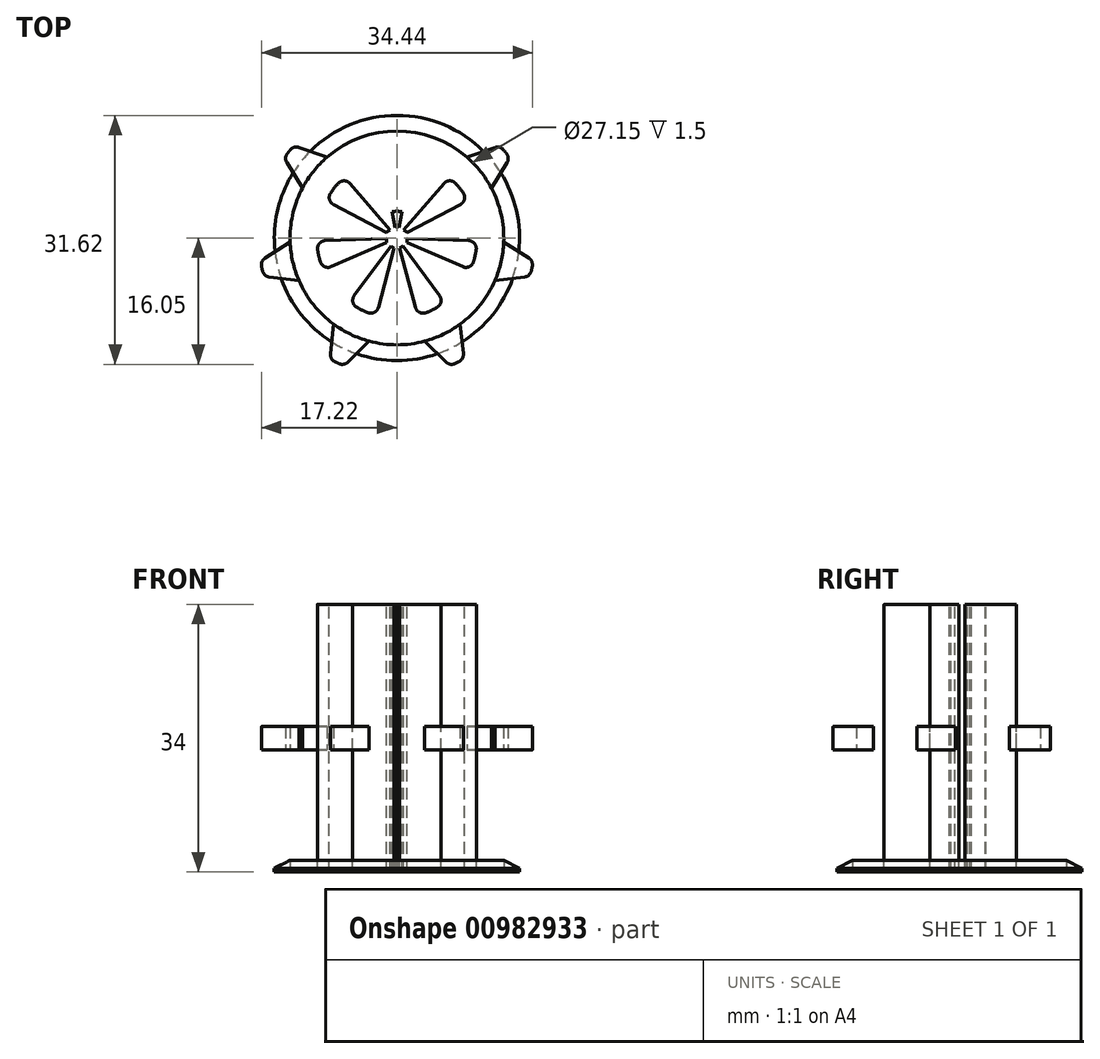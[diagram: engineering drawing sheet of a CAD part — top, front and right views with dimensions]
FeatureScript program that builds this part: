
annotation { "Feature Type Name" : "Feature", "Feature Type Description" : "" }
export const myFeature = defineFeature(function(context is Context, id is Id, definition is map)
    precondition{}
    {
        {
            var Q0;
            Q0=qCreatedBy(makeId("Top.planeOp"),FACE);
            var sketch = newSketch(context, id + "F0", { "sketchPlane" : qUnion([Q0])});
            skCircle(sketch, "E0", {"center": v(0, 0) * mm, "radius": 13.57 * mm});
            skSolve(sketch);
        }
        {
            var Q0;
            Q0=makeQuery(id+"F0.imprint","IMPRINT",FACE,{"disambiguationData":[TD([[makeQuery(id+"F0.imprint","IMPRINT",EDGE,{"derivedFrom":sQuery(id+"F0.wireOp",EDGE,"E0")}),1.0]])]});
            extrude(context, id + "F1", {"entities" : qUnion([Q0]), "endBound" : BoundingType.SYMMETRIC, "depth" : 34 * mm, "offsetDistance" : 25 * mm});
        }
        {
            var Q0;
            Q0=qCreatedBy(makeId("Top.planeOp"),FACE);
            var sketch = newSketch(context, id + "F2", { "sketchPlane" : qUnion([Q0])});
            skPoint(sketch, "E1", {"position": v(0, 17.57) * mm});
            skPoint(sketch, "E2", {"position": v(15.3, 12.2) * mm});
            skPoint(sketch, "E3", {"position": v(19.08, -4.36) * mm});
            skPoint(sketch, "E4", {"position": v(8.5, -17.64) * mm});
            skPoint(sketch, "E5", {"position": v(-8.5, -17.64) * mm});
            skPoint(sketch, "E6", {"position": v(-19.08, -4.36) * mm});
            skPoint(sketch, "E7", {"position": v(-15.3, 12.2) * mm});
            skArc(sketch, "E8", {"start": v(-1, 17.55) * mm, "mid": v(0, 17.57) * mm, "end": v(1, 17.55) * mm});
            skPoint(sketch, "E9", {"position": v(-12.18, 9.71) * mm});
            skPoint(sketch, "E10", {"position": v(12.18, 9.71) * mm});
            skPoint(sketch, "E11", {"position": v(15.18, -3.47) * mm});
            skPoint(sketch, "E12", {"position": v(6.76, -14.03) * mm});
            skPoint(sketch, "E13", {"position": v(-6.76, -14.03) * mm});
            skPoint(sketch, "E14", {"position": v(-15.18, -3.47) * mm});
            skPoint(sketch, "E15", {"position": v(0, 13.57) * mm});
            skArc(sketch, "E16", {"start": v(-2.5, 13.34) * mm, "mid": v(0, 13.57) * mm, "end": v(2.5, 13.34) * mm});
            skLineSegment(sketch, "E17", {"start": v(-2.5, 13.34) * mm, "end": v(-1, 17.55) * mm});
            skLineSegment(sketch, "E18", {"start": v(1, 17.55) * mm, "end": v(2.5, 13.34) * mm});
            skLineSegment(sketch, "E19.1.0", {"start": v(14.34, 10.16) * mm, "end": v(11.99, 6.36) * mm});
            skArc(sketch, "E19.1.1", {"start": v(8.87, 10.27) * mm, "mid": v(10.61, 8.46) * mm, "end": v(11.99, 6.36) * mm});
            skLineSegment(sketch, "E19.1.2", {"start": v(8.87, 10.27) * mm, "end": v(13.1, 11.72) * mm});
            skArc(sketch, "E19.1.3", {"start": v(13.1, 11.72) * mm, "mid": v(13.74, 10.96) * mm, "end": v(14.34, 10.16) * mm});
            skLineSegment(sketch, "E19.2.0", {"start": v(16.88, -4.88) * mm, "end": v(12.45, -5.4) * mm});
            skArc(sketch, "E19.2.1", {"start": v(13.56, -0.53) * mm, "mid": v(13.23, -3.02) * mm, "end": v(12.45, -5.4) * mm});
            skLineSegment(sketch, "E19.2.2", {"start": v(13.56, -0.53) * mm, "end": v(17.33, -2.93) * mm});
            skArc(sketch, "E19.2.3", {"start": v(17.33, -2.93) * mm, "mid": v(17.13, -3.91) * mm, "end": v(16.88, -4.88) * mm});
            skLineSegment(sketch, "E19.3.0", {"start": v(6.71, -16.24) * mm, "end": v(3.54, -13.1) * mm});
            skArc(sketch, "E19.3.1", {"start": v(8.04, -10.94) * mm, "mid": v(5.89, -12.23) * mm, "end": v(3.54, -13.1) * mm});
            skLineSegment(sketch, "E19.3.2", {"start": v(8.04, -10.94) * mm, "end": v(8.51, -15.37) * mm});
            skArc(sketch, "E19.3.3", {"start": v(8.51, -15.37) * mm, "mid": v(7.63, -15.83) * mm, "end": v(6.71, -16.24) * mm});
            skLineSegment(sketch, "E19.4.0", {"start": v(-8.51, -15.37) * mm, "end": v(-8.04, -10.94) * mm});
            skArc(sketch, "E19.4.1", {"start": v(-3.54, -13.1) * mm, "mid": v(-5.89, -12.23) * mm, "end": v(-8.04, -10.94) * mm});
            skLineSegment(sketch, "E19.4.2", {"start": v(-3.54, -13.1) * mm, "end": v(-6.71, -16.24) * mm});
            skArc(sketch, "E19.4.3", {"start": v(-6.71, -16.24) * mm, "mid": v(-7.63, -15.83) * mm, "end": v(-8.51, -15.37) * mm});
            skLineSegment(sketch, "E19.5.0", {"start": v(-17.33, -2.93) * mm, "end": v(-13.56, -0.53) * mm});
            skArc(sketch, "E19.5.1", {"start": v(-12.45, -5.4) * mm, "mid": v(-13.23, -3.02) * mm, "end": v(-13.56, -0.53) * mm});
            skLineSegment(sketch, "E19.5.2", {"start": v(-12.45, -5.4) * mm, "end": v(-16.88, -4.88) * mm});
            skArc(sketch, "E19.5.3", {"start": v(-16.88, -4.88) * mm, "mid": v(-17.13, -3.91) * mm, "end": v(-17.33, -2.93) * mm});
            skLineSegment(sketch, "E19.6.0", {"start": v(-13.1, 11.72) * mm, "end": v(-8.87, 10.27) * mm});
            skArc(sketch, "E19.6.1", {"start": v(-11.99, 6.36) * mm, "mid": v(-10.61, 8.46) * mm, "end": v(-8.87, 10.27) * mm});
            skLineSegment(sketch, "E19.6.2", {"start": v(-11.99, 6.36) * mm, "end": v(-14.34, 10.16) * mm});
            skArc(sketch, "E19.6.3", {"start": v(-14.34, 10.16) * mm, "mid": v(-13.74, 10.96) * mm, "end": v(-13.1, 11.72) * mm});
            skLineSegment(sketch, "E19.anchor1", {"start": v(0, 0) * mm, "end": v(2.5, 13.34) * mm, "construction": true});
            skLineSegment(sketch, "E19.anchor2", {"start": v(0, 0) * mm, "end": v(-8.87, 10.27) * mm, "construction": true});
            skSolve(sketch);
        }
        {
            var Q0;
            Q0=makeQuery(id+"F2.imprint","IMPRINT",FACE,{"disambiguationData":[TD([[makeQuery(id+"F2.imprint","IMPRINT",EDGE,{"derivedFrom":sQuery(id+"F2.wireOp",EDGE,"E19.6.0")}),-1.0]])]});
            var Q1;
            Q1=makeQuery(id+"F2.imprint","IMPRINT",FACE,{"disambiguationData":[TD([[makeQuery(id+"F2.imprint","IMPRINT",EDGE,{"derivedFrom":sQuery(id+"F2.wireOp",EDGE,"E8")}),-1.0]])]});
            var Q2;
            Q2=makeQuery(id+"F2.imprint","IMPRINT",FACE,{"disambiguationData":[TD([[makeQuery(id+"F2.imprint","IMPRINT",EDGE,{"derivedFrom":sQuery(id+"F2.wireOp",EDGE,"E19.1.0")}),-1.0]])]});
            var Q3;
            Q3=makeQuery(id+"F2.imprint","IMPRINT",FACE,{"disambiguationData":[TD([[makeQuery(id+"F2.imprint","IMPRINT",EDGE,{"derivedFrom":sQuery(id+"F2.wireOp",EDGE,"E19.2.0")}),-1.0]])]});
            var Q4;
            Q4=makeQuery(id+"F2.imprint","IMPRINT",FACE,{"disambiguationData":[TD([[makeQuery(id+"F2.imprint","IMPRINT",EDGE,{"derivedFrom":sQuery(id+"F2.wireOp",EDGE,"E19.3.0")}),-1.0]])]});
            var Q5;
            Q5=makeQuery(id+"F2.imprint","IMPRINT",FACE,{"disambiguationData":[TD([[makeQuery(id+"F2.imprint","IMPRINT",EDGE,{"derivedFrom":sQuery(id+"F2.wireOp",EDGE,"E19.4.0")}),-1.0]])]});
            var Q6;
            Q6=makeQuery(id+"F2.imprint","IMPRINT",FACE,{"disambiguationData":[TD([[makeQuery(id+"F2.imprint","IMPRINT",EDGE,{"derivedFrom":sQuery(id+"F2.wireOp",EDGE,"E19.5.0")}),-1.0]])]});
            extrude(context, id + "F3", {"entities" : qUnion([Q0, Q1, Q2, Q3, Q4, Q5, Q6]), "operationType" : NewBodyOperationType.ADD, "endBound" : BoundingType.SYMMETRIC, "depth" : 3 * mm, "offsetDistance" : 25 * mm});
        }
        {
            var Q0;
            Q0=makeQuery(id+"F1.opExtrude","CAP_FACE",FACE,{"disambiguationData":[OSD([sQuery(id+"F0.wireOp",EDGE,"E0")])],"isStart":false});
            var sketch = newSketch(context, id + "F4", { "sketchPlane" : qUnion([Q0])});
            skLineSegment(sketch, "E20", {"start": v(0, 0) * mm, "end": v(0, 3.4) * mm});
            skLineSegment(sketch, "E21", {"start": v(0, 3.4) * mm, "end": v(0, 6.79) * mm});
            skLineSegment(sketch, "E22", {"start": v(0, 6.79) * mm, "end": v(0, 10.18) * mm});
            skLineSegment(sketch, "E23", {"start": v(0, 10.18) * mm, "end": v(0, 13.57) * mm});
            skArc(sketch, "E24", {"start": v(-1.9, 10) * mm, "mid": v(0, 10.18) * mm, "end": v(1.9, 10) * mm});
            skPoint(sketch, "E25", {"position": v(0, 10.18) * mm});
            skArc(sketch, "E26", {"start": v(-0.63, 3.33) * mm, "mid": v(0, 3.4) * mm, "end": v(0.63, 3.33) * mm});
            skPoint(sketch, "E27", {"position": v(0, 3.4) * mm});
            skLineSegment(sketch, "E28", {"start": v(0, 0) * mm, "end": v(-1.9, 10) * mm});
            skLineSegment(sketch, "E29", {"start": v(1.9, 10) * mm, "end": v(0, 0) * mm});
            skArc(sketch, "E30.1.0", {"start": v(-9, 4.75) * mm, "mid": v(-7.96, 6.35) * mm, "end": v(-6.64, 7.72) * mm});
            skLineSegment(sketch, "E30.1.1", {"start": v(-6.64, 7.72) * mm, "end": v(0, 0) * mm});
            skArc(sketch, "E30.1.2", {"start": v(-3, 1.58) * mm, "mid": v(-2.65, 2.12) * mm, "end": v(-2.21, 2.57) * mm});
            skLineSegment(sketch, "E30.1.3", {"start": v(0, 0) * mm, "end": v(-9, 4.75) * mm});
            skArc(sketch, "E30.2.0", {"start": v(-9.33, -4.07) * mm, "mid": v(-9.93, -2.27) * mm, "end": v(-10.17, -0.38) * mm});
            skLineSegment(sketch, "E30.2.1", {"start": v(-10.17, -0.38) * mm, "end": v(0, 0) * mm});
            skArc(sketch, "E30.2.2", {"start": v(-3.1, -1.36) * mm, "mid": v(-3.3, -0.76) * mm, "end": v(-3.4, -0.13) * mm});
            skLineSegment(sketch, "E30.2.3", {"start": v(0, 0) * mm, "end": v(-9.33, -4.07) * mm});
            skArc(sketch, "E30.3.0", {"start": v(-2.63, -9.83) * mm, "mid": v(-4.42, -9.17) * mm, "end": v(-6.05, -8.19) * mm});
            skLineSegment(sketch, "E30.3.1", {"start": v(-6.05, -8.19) * mm, "end": v(0, 0) * mm});
            skArc(sketch, "E30.3.2", {"start": v(-0.88, -3.28) * mm, "mid": v(-1.47, -3.06) * mm, "end": v(-2.02, -2.73) * mm});
            skLineSegment(sketch, "E30.3.3", {"start": v(0, 0) * mm, "end": v(-2.63, -9.83) * mm});
            skArc(sketch, "E30.4.0", {"start": v(6.05, -8.19) * mm, "mid": v(4.42, -9.17) * mm, "end": v(2.63, -9.83) * mm});
            skLineSegment(sketch, "E30.4.1", {"start": v(2.63, -9.83) * mm, "end": v(0, 0) * mm});
            skArc(sketch, "E30.4.2", {"start": v(2.02, -2.73) * mm, "mid": v(1.47, -3.06) * mm, "end": v(0.88, -3.28) * mm});
            skLineSegment(sketch, "E30.4.3", {"start": v(0, 0) * mm, "end": v(6.05, -8.19) * mm});
            skArc(sketch, "E30.5.0", {"start": v(10.17, -0.38) * mm, "mid": v(9.93, -2.27) * mm, "end": v(9.33, -4.07) * mm});
            skLineSegment(sketch, "E30.5.1", {"start": v(9.33, -4.07) * mm, "end": v(0, 0) * mm});
            skArc(sketch, "E30.5.2", {"start": v(3.4, -0.13) * mm, "mid": v(3.3, -0.76) * mm, "end": v(3.1, -1.36) * mm});
            skLineSegment(sketch, "E30.5.3", {"start": v(0, 0) * mm, "end": v(10.17, -0.38) * mm});
            skArc(sketch, "E30.6.0", {"start": v(6.64, 7.72) * mm, "mid": v(7.96, 6.35) * mm, "end": v(9, 4.75) * mm});
            skLineSegment(sketch, "E30.6.1", {"start": v(9, 4.75) * mm, "end": v(0, 0) * mm});
            skArc(sketch, "E30.6.2", {"start": v(2.21, 2.57) * mm, "mid": v(2.65, 2.12) * mm, "end": v(3, 1.58) * mm});
            skLineSegment(sketch, "E30.6.3", {"start": v(0, 0) * mm, "end": v(6.64, 7.72) * mm});
            skCircle(sketch, "E31.cCircle", {"center": v(0, 0) * mm, "radius": 1.5 * mm, "construction": true});
            skLineSegment(sketch, "E31.0", {"start": v(0, 1.5) * mm, "end": v(1.3, 0.75) * mm});
            skLineSegment(sketch, "E31.1", {"start": v(1.3, 0.75) * mm, "end": v(1.3, -0.75) * mm});
            skLineSegment(sketch, "E31.2", {"start": v(1.3, -0.75) * mm, "end": v(0, -1.5) * mm});
            skLineSegment(sketch, "E31.3", {"start": v(0, -1.5) * mm, "end": v(-1.3, -0.75) * mm});
            skLineSegment(sketch, "E31.4", {"start": v(-1.3, -0.75) * mm, "end": v(-1.3, 0.75) * mm});
            skLineSegment(sketch, "E31.5", {"start": v(-1.3, 0.75) * mm, "end": v(0, 1.5) * mm});
            skSolve(sketch);
        }
        {
            var Q0;
            {var subQ0=sQuery(id+"F4.wireOp",EDGE,"E30.1.0");Q0=makeQuery(id+"F4.imprint","IMPRINT",FACE,{"disambiguationData":[TD([[makeQuery(id+"F4.imprint","IMPRINT",EDGE,{"derivedFrom":subQ0}),-1.0]])]});}
            var Q1;
            {var subQ1=sQuery(id+"F4.wireOp",EDGE,"E21");Q1=makeQuery(id+"F4.imprint","IMPRINT",FACE,{"disambiguationData":[TD([[makeQuery(id+"F4.imprint","IMPRINT",EDGE,{"derivedFrom":subQ1}),1.0]])]});}
            var Q2;
            {var subQ5=sQuery(id+"F4.wireOp",EDGE,"E21");Q2=makeQuery(id+"F4.imprint","IMPRINT",FACE,{"disambiguationData":[TD([[makeQuery(id+"F4.imprint","IMPRINT",EDGE,{"derivedFrom":subQ5}),-1.0]])]});}
            var Q3;
            {var subQ0=sQuery(id+"F4.wireOp",EDGE,"E30.6.0");Q3=makeQuery(id+"F4.imprint","IMPRINT",FACE,{"disambiguationData":[TD([[makeQuery(id+"F4.imprint","IMPRINT",EDGE,{"derivedFrom":subQ0}),-1.0]])]});}
            var Q4;
            {var subQ0=sQuery(id+"F4.wireOp",EDGE,"E30.5.0");Q4=makeQuery(id+"F4.imprint","IMPRINT",FACE,{"disambiguationData":[TD([[makeQuery(id+"F4.imprint","IMPRINT",EDGE,{"derivedFrom":subQ0}),-1.0]])]});}
            var Q5;
            {var subQ0=sQuery(id+"F4.wireOp",EDGE,"E30.4.0");Q5=makeQuery(id+"F4.imprint","IMPRINT",FACE,{"disambiguationData":[TD([[makeQuery(id+"F4.imprint","IMPRINT",EDGE,{"derivedFrom":subQ0}),-1.0]])]});}
            var Q6;
            {var subQ0=sQuery(id+"F4.wireOp",EDGE,"E30.3.0");Q6=makeQuery(id+"F4.imprint","IMPRINT",FACE,{"disambiguationData":[TD([[makeQuery(id+"F4.imprint","IMPRINT",EDGE,{"derivedFrom":subQ0}),-1.0]])]});}
            var Q7;
            {var subQ0=sQuery(id+"F4.wireOp",EDGE,"E30.2.0");Q7=makeQuery(id+"F4.imprint","IMPRINT",FACE,{"disambiguationData":[TD([[makeQuery(id+"F4.imprint","IMPRINT",EDGE,{"derivedFrom":subQ0}),-1.0]])]});}
            var Q8;
            {var subQ3=sQuery(id+"F4.wireOp",EDGE,"E31.5");var subQ5=sQuery(id+"F4.wireOp",EDGE,"E31.4");var subQ7=makeQuery(id+"F4.imprint","INTERSECT",VERTEX,{"derivedFrom":[subQ5,subQ3]});Q8=makeQuery(id+"F4.imprint","IMPRINT",FACE,{"disambiguationData":[TD([[makeQuery(id+"F4.imprint","IMPRINT",EDGE,{"disambiguationData":[TD([[subQ7,1.0]])],"derivedFrom":subQ5}),-1.0]])]});}
            var Q9;
            {var subQ1=sQuery(id+"F4.wireOp",EDGE,"E28");var subQ3=sQuery(id+"F4.wireOp",EDGE,"E31.5");var subQ4=makeQuery(id+"F4.imprint","INTERSECT",VERTEX,{"derivedFrom":[subQ1,subQ3]});Q9=makeQuery(id+"F4.imprint","IMPRINT",FACE,{"disambiguationData":[TD([[makeQuery(id+"F4.imprint","IMPRINT",EDGE,{"disambiguationData":[TD([[subQ4,1.0]])],"derivedFrom":subQ3}),-1.0]])]});}
            var Q10;
            {var subQ0=sQuery(id+"F4.wireOp",EDGE,"E28");var subQ3=sQuery(id+"F4.wireOp",EDGE,"E31.5");var subQ5=makeQuery(id+"F4.imprint","INTERSECT",VERTEX,{"derivedFrom":[subQ0,subQ3]});Q10=makeQuery(id+"F4.imprint","IMPRINT",FACE,{"disambiguationData":[TD([[makeQuery(id+"F4.imprint","IMPRINT",EDGE,{"disambiguationData":[TD([[subQ5,-1.0]])],"derivedFrom":subQ3}),-1.0]])]});}
            var Q11;
            {var subQ0=sQuery(id+"F4.wireOp",EDGE,"E29");var subQ3=sQuery(id+"F4.wireOp",EDGE,"E31.0");var subQ5=makeQuery(id+"F4.imprint","INTERSECT",VERTEX,{"derivedFrom":[subQ0,subQ3]});Q11=makeQuery(id+"F4.imprint","IMPRINT",FACE,{"disambiguationData":[TD([[makeQuery(id+"F4.imprint","IMPRINT",EDGE,{"disambiguationData":[TD([[subQ5,1.0]])],"derivedFrom":subQ3}),-1.0]])]});}
            var Q12;
            {var subQ1=sQuery(id+"F4.wireOp",EDGE,"E29");var subQ3=sQuery(id+"F4.wireOp",EDGE,"E31.0");var subQ4=makeQuery(id+"F4.imprint","INTERSECT",VERTEX,{"derivedFrom":[subQ1,subQ3]});Q12=makeQuery(id+"F4.imprint","IMPRINT",FACE,{"disambiguationData":[TD([[makeQuery(id+"F4.imprint","IMPRINT",EDGE,{"disambiguationData":[TD([[subQ4,-1.0]])],"derivedFrom":subQ3}),-1.0]])]});}
            var Q13;
            {var subQ3=sQuery(id+"F4.wireOp",EDGE,"E31.1");var subQ5=sQuery(id+"F4.wireOp",EDGE,"E31.0");var subQ7=makeQuery(id+"F4.imprint","INTERSECT",VERTEX,{"derivedFrom":[subQ5,subQ3]});Q13=makeQuery(id+"F4.imprint","IMPRINT",FACE,{"disambiguationData":[TD([[makeQuery(id+"F4.imprint","IMPRINT",EDGE,{"disambiguationData":[TD([[subQ7,1.0]])],"derivedFrom":subQ5}),-1.0]])]});}
            var Q14;
            {var subQ1=sQuery(id+"F4.wireOp",EDGE,"E30.5.3");var subQ3=sQuery(id+"F4.wireOp",EDGE,"E31.1");var subQ4=makeQuery(id+"F4.imprint","INTERSECT",VERTEX,{"derivedFrom":[subQ1,subQ3]});Q14=makeQuery(id+"F4.imprint","IMPRINT",FACE,{"disambiguationData":[TD([[makeQuery(id+"F4.imprint","IMPRINT",EDGE,{"disambiguationData":[TD([[subQ4,1.0]])],"derivedFrom":subQ3}),-1.0]])]});}
            var Q15;
            {var subQ1=sQuery(id+"F4.wireOp",EDGE,"E30.5.1");var subQ3=sQuery(id+"F4.wireOp",EDGE,"E31.1");var subQ4=makeQuery(id+"F4.imprint","INTERSECT",VERTEX,{"derivedFrom":[subQ1,subQ3]});Q15=makeQuery(id+"F4.imprint","IMPRINT",FACE,{"disambiguationData":[TD([[makeQuery(id+"F4.imprint","IMPRINT",EDGE,{"disambiguationData":[TD([[subQ4,1.0]])],"derivedFrom":subQ3}),-1.0]])]});}
            var Q16;
            {var subQ3=sQuery(id+"F4.wireOp",EDGE,"E31.2");var subQ5=sQuery(id+"F4.wireOp",EDGE,"E31.1");var subQ6=makeQuery(id+"F4.imprint","INTERSECT",VERTEX,{"derivedFrom":[subQ5,subQ3]});Q16=makeQuery(id+"F4.imprint","IMPRINT",FACE,{"disambiguationData":[TD([[makeQuery(id+"F4.imprint","IMPRINT",EDGE,{"disambiguationData":[TD([[subQ6,1.0]])],"derivedFrom":subQ5}),-1.0]])]});}
            var Q17;
            {var subQ1=sQuery(id+"F4.wireOp",EDGE,"E30.4.1");var subQ3=sQuery(id+"F4.wireOp",EDGE,"E31.2");var subQ4=makeQuery(id+"F4.imprint","INTERSECT",VERTEX,{"derivedFrom":[subQ1,subQ3]});Q17=makeQuery(id+"F4.imprint","IMPRINT",FACE,{"disambiguationData":[TD([[makeQuery(id+"F4.imprint","IMPRINT",EDGE,{"disambiguationData":[TD([[subQ4,1.0]])],"derivedFrom":subQ3}),-1.0]])]});}
            var Q18;
            {var subQ3=sQuery(id+"F4.wireOp",EDGE,"E31.3");var subQ5=sQuery(id+"F4.wireOp",EDGE,"E31.2");var subQ7=makeQuery(id+"F4.imprint","INTERSECT",VERTEX,{"derivedFrom":[subQ5,subQ3]});Q18=makeQuery(id+"F4.imprint","IMPRINT",FACE,{"disambiguationData":[TD([[makeQuery(id+"F4.imprint","IMPRINT",EDGE,{"disambiguationData":[TD([[subQ7,1.0]])],"derivedFrom":subQ5}),-1.0]])]});}
            var Q19;
            {var subQ1=sQuery(id+"F4.wireOp",EDGE,"E30.3.1");var subQ3=sQuery(id+"F4.wireOp",EDGE,"E31.3");var subQ4=makeQuery(id+"F4.imprint","INTERSECT",VERTEX,{"derivedFrom":[subQ1,subQ3]});Q19=makeQuery(id+"F4.imprint","IMPRINT",FACE,{"disambiguationData":[TD([[makeQuery(id+"F4.imprint","IMPRINT",EDGE,{"disambiguationData":[TD([[subQ4,1.0]])],"derivedFrom":subQ3}),-1.0]])]});}
            var Q20;
            {var subQ3=sQuery(id+"F4.wireOp",EDGE,"E31.4");var subQ5=sQuery(id+"F4.wireOp",EDGE,"E31.3");var subQ7=makeQuery(id+"F4.imprint","INTERSECT",VERTEX,{"derivedFrom":[subQ5,subQ3]});Q20=makeQuery(id+"F4.imprint","IMPRINT",FACE,{"disambiguationData":[TD([[makeQuery(id+"F4.imprint","IMPRINT",EDGE,{"disambiguationData":[TD([[subQ7,1.0]])],"derivedFrom":subQ5}),-1.0]])]});}
            var Q21;
            {var subQ1=sQuery(id+"F4.wireOp",EDGE,"E30.2.1");var subQ3=sQuery(id+"F4.wireOp",EDGE,"E31.4");var subQ4=makeQuery(id+"F4.imprint","INTERSECT",VERTEX,{"derivedFrom":[subQ1,subQ3]});Q21=makeQuery(id+"F4.imprint","IMPRINT",FACE,{"disambiguationData":[TD([[makeQuery(id+"F4.imprint","IMPRINT",EDGE,{"disambiguationData":[TD([[subQ4,1.0]])],"derivedFrom":subQ3}),-1.0]])]});}
            var Q22;
            {var subQ1=sQuery(id+"F4.wireOp",EDGE,"E30.1.3");var subQ3=sQuery(id+"F4.wireOp",EDGE,"E31.4");var subQ4=makeQuery(id+"F4.imprint","INTERSECT",VERTEX,{"derivedFrom":[subQ1,subQ3]});Q22=makeQuery(id+"F4.imprint","IMPRINT",FACE,{"disambiguationData":[TD([[makeQuery(id+"F4.imprint","IMPRINT",EDGE,{"disambiguationData":[TD([[subQ4,1.0]])],"derivedFrom":subQ3}),-1.0]])]});}
            extrude(context, id + "F5", {"entities" : qUnion([Q0, Q1, Q2, Q3, Q4, Q5, Q6, Q7, Q8, Q9, Q10, Q11, Q12, Q13, Q14, Q15, Q16, Q17, Q18, Q19, Q20, Q21, Q22]), "operationType" : NewBodyOperationType.REMOVE, "oppositeDirection" : true, "depth" : 34 * mm, "offsetDistance" : 25 * mm});
        }
        {
            var Q0;
            Q0=makeQuery(id+"F5.boolean.opBoolean","COPY",EDGE,{"derivedFrom":makeQuery(id+"F5.opExtrude","SWEPT_EDGE",EDGE,{"disambiguationData":[OSD([sQuery(id+"F4.wireOp",EDGE,"E30.3.0"),sQuery(id+"F4.wireOp",EDGE,"E30.3.1")])]})});
            var Q1;
            Q1=makeQuery(id+"F5.boolean.opBoolean","COPY",EDGE,{"derivedFrom":makeQuery(id+"F5.opExtrude","SWEPT_EDGE",EDGE,{"disambiguationData":[OSD([sQuery(id+"F4.wireOp",EDGE,"E30.3.0"),sQuery(id+"F4.wireOp",EDGE,"E30.3.3")])]})});
            var Q2;
            Q2=makeQuery(id+"F5.boolean.opBoolean","COPY",EDGE,{"derivedFrom":makeQuery(id+"F5.opExtrude","SWEPT_EDGE",EDGE,{"disambiguationData":[OSD([sQuery(id+"F4.wireOp",EDGE,"E30.4.0"),sQuery(id+"F4.wireOp",EDGE,"E30.4.1")])]})});
            var Q3;
            Q3=makeQuery(id+"F5.boolean.opBoolean","COPY",EDGE,{"derivedFrom":makeQuery(id+"F5.opExtrude","SWEPT_EDGE",EDGE,{"disambiguationData":[OSD([sQuery(id+"F4.wireOp",EDGE,"E30.4.0"),sQuery(id+"F4.wireOp",EDGE,"E30.4.3")])]})});
            var Q4;
            Q4=makeQuery(id+"F5.boolean.opBoolean","COPY",EDGE,{"derivedFrom":makeQuery(id+"F5.opExtrude","SWEPT_EDGE",EDGE,{"disambiguationData":[OSD([sQuery(id+"F4.wireOp",EDGE,"E30.5.0"),sQuery(id+"F4.wireOp",EDGE,"E30.5.1")])]})});
            var Q5;
            Q5=makeQuery(id+"F5.boolean.opBoolean","COPY",EDGE,{"derivedFrom":makeQuery(id+"F5.opExtrude","SWEPT_EDGE",EDGE,{"disambiguationData":[OSD([sQuery(id+"F4.wireOp",EDGE,"E30.2.0"),sQuery(id+"F4.wireOp",EDGE,"E30.2.3")])]})});
            var Q6;
            Q6=makeQuery(id+"F5.boolean.opBoolean","COPY",EDGE,{"derivedFrom":makeQuery(id+"F5.opExtrude","SWEPT_EDGE",EDGE,{"disambiguationData":[OSD([sQuery(id+"F4.wireOp",EDGE,"E30.2.0"),sQuery(id+"F4.wireOp",EDGE,"E30.2.1")])]})});
            var Q7;
            Q7=makeQuery(id+"F5.boolean.opBoolean","COPY",EDGE,{"derivedFrom":makeQuery(id+"F5.opExtrude","SWEPT_EDGE",EDGE,{"disambiguationData":[OSD([sQuery(id+"F4.wireOp",EDGE,"E30.1.0"),sQuery(id+"F4.wireOp",EDGE,"E30.1.3")])]})});
            var Q8;
            Q8=makeQuery(id+"F5.boolean.opBoolean","COPY",EDGE,{"derivedFrom":makeQuery(id+"F5.opExtrude","SWEPT_EDGE",EDGE,{"disambiguationData":[OSD([sQuery(id+"F4.wireOp",EDGE,"E30.1.0"),sQuery(id+"F4.wireOp",EDGE,"E30.1.1")])]})});
            var Q9;
            Q9=makeQuery(id+"F5.boolean.opBoolean","COPY",EDGE,{"derivedFrom":makeQuery(id+"F5.opExtrude","SWEPT_EDGE",EDGE,{"disambiguationData":[OSD([sQuery(id+"F4.wireOp",EDGE,"E30.6.0"),sQuery(id+"F4.wireOp",EDGE,"E30.6.3")])]})});
            var Q10;
            Q10=makeQuery(id+"F5.boolean.opBoolean","COPY",EDGE,{"derivedFrom":makeQuery(id+"F5.opExtrude","SWEPT_EDGE",EDGE,{"disambiguationData":[OSD([sQuery(id+"F4.wireOp",EDGE,"E24"),sQuery(id+"F4.wireOp",EDGE,"E28")])]})});
            var Q11;
            Q11=makeQuery(id+"F5.boolean.opBoolean","COPY",EDGE,{"derivedFrom":makeQuery(id+"F5.opExtrude","SWEPT_EDGE",EDGE,{"disambiguationData":[OSD([sQuery(id+"F4.wireOp",EDGE,"E24"),sQuery(id+"F4.wireOp",EDGE,"E29")])]})});
            var Q12;
            Q12=makeQuery(id+"F5.boolean.opBoolean","COPY",EDGE,{"derivedFrom":makeQuery(id+"F5.opExtrude","SWEPT_EDGE",EDGE,{"disambiguationData":[OSD([sQuery(id+"F4.wireOp",EDGE,"E30.6.0"),sQuery(id+"F4.wireOp",EDGE,"E30.6.1")])]})});
            var Q13;
            Q13=makeQuery(id+"F5.boolean.opBoolean","COPY",EDGE,{"derivedFrom":makeQuery(id+"F5.opExtrude","SWEPT_EDGE",EDGE,{"disambiguationData":[OSD([sQuery(id+"F4.wireOp",EDGE,"E30.5.0"),sQuery(id+"F4.wireOp",EDGE,"E30.5.3")])]})});
            fillet(context, id + "F6", {"entities" : qUnion([Q0, Q1, Q2, Q3, Q4, Q5, Q6, Q7, Q8, Q9, Q10, Q11, Q12, Q13]), "radius" : 1 * mm, "tangentPropagation" : true, "allowEdgeOverflow" : false});
        }
        {
            var Q0;
            Q0=makeQuery(id+"F1.opExtrude","CAP_FACE",FACE,{"disambiguationData":[OSD([sQuery(id+"F0.wireOp",EDGE,"E0")])],"isStart":true});
            var sketch = newSketch(context, id + "F7", { "sketchPlane" : qUnion([Q0])});
            skCircle(sketch, "E32", {"center": v(0, 0) * mm, "radius": 13.57 * mm});
            skCircle(sketch, "E33", {"center": v(0, 0) * mm, "radius": 15.57 * mm});
            skSolve(sketch);
        }
        {
            var Q0;
            Q0=qSketchRegion(id+"F7",true);
            extrude(context, id + "F8", {"entities" : qUnion([Q0]), "operationType" : NewBodyOperationType.ADD, "oppositeDirection" : true, "depth" : 1.5 * mm, "offsetDistance" : 25 * mm});
        }
        {
            var Q0;
            Q0=makeQuery(id+"F8.opExtrude","CAP_EDGE",EDGE,{"disambiguationData":[OSD([sQuery(id+"F7.wireOp",EDGE,"E33")])],"isStart":false});
            chamfer(context, id + "F9", {"entities" : qUnion([Q0]), "chamferType" : ChamferType.TWO_OFFSETS, "width1" : 2 * mm, "oppositeDirection" : true, "width2" : 1 * mm, "tangentPropagation" : true});
        }
        {
            var Q0;
            Q0=makeQuery(id+"F3.opExtrude","SWEPT_EDGE",EDGE,{"disambiguationData":[OSD([sQuery(id+"F2.wireOp",EDGE,"E19.1.0"),sQuery(id+"F2.wireOp",EDGE,"E19.1.3")])]});
            var Q1;
            Q1=makeQuery(id+"F3.opExtrude","SWEPT_EDGE",EDGE,{"disambiguationData":[OSD([sQuery(id+"F2.wireOp",EDGE,"E19.1.2"),sQuery(id+"F2.wireOp",EDGE,"E19.1.3")])]});
            var Q2;
            Q2=makeQuery(id+"F3.opExtrude","SWEPT_EDGE",EDGE,{"disambiguationData":[OSD([sQuery(id+"F2.wireOp",EDGE,"E8"),sQuery(id+"F2.wireOp",EDGE,"E18")])]});
            var Q3;
            Q3=makeQuery(id+"F3.opExtrude","SWEPT_EDGE",EDGE,{"disambiguationData":[OSD([sQuery(id+"F2.wireOp",EDGE,"E8"),sQuery(id+"F2.wireOp",EDGE,"E17")])]});
            var Q4;
            Q4=makeQuery(id+"F3.opExtrude","SWEPT_EDGE",EDGE,{"disambiguationData":[OSD([sQuery(id+"F2.wireOp",EDGE,"E19.6.0"),sQuery(id+"F2.wireOp",EDGE,"E19.6.3")])]});
            var Q5;
            Q5=makeQuery(id+"F3.opExtrude","SWEPT_EDGE",EDGE,{"disambiguationData":[OSD([sQuery(id+"F2.wireOp",EDGE,"E19.6.2"),sQuery(id+"F2.wireOp",EDGE,"E19.6.3")])]});
            var Q6;
            Q6=makeQuery(id+"F3.opExtrude","SWEPT_EDGE",EDGE,{"disambiguationData":[OSD([sQuery(id+"F2.wireOp",EDGE,"E19.5.0"),sQuery(id+"F2.wireOp",EDGE,"E19.5.3")])]});
            var Q7;
            Q7=makeQuery(id+"F3.opExtrude","SWEPT_EDGE",EDGE,{"disambiguationData":[OSD([sQuery(id+"F2.wireOp",EDGE,"E19.5.2"),sQuery(id+"F2.wireOp",EDGE,"E19.5.3")])]});
            var Q8;
            Q8=makeQuery(id+"F3.opExtrude","SWEPT_EDGE",EDGE,{"disambiguationData":[OSD([sQuery(id+"F2.wireOp",EDGE,"E19.4.0"),sQuery(id+"F2.wireOp",EDGE,"E19.4.3")])]});
            var Q9;
            Q9=makeQuery(id+"F3.opExtrude","SWEPT_EDGE",EDGE,{"disambiguationData":[OSD([sQuery(id+"F2.wireOp",EDGE,"E19.4.2"),sQuery(id+"F2.wireOp",EDGE,"E19.4.3")])]});
            var Q10;
            Q10=makeQuery(id+"F3.opExtrude","SWEPT_EDGE",EDGE,{"disambiguationData":[OSD([sQuery(id+"F2.wireOp",EDGE,"E19.3.0"),sQuery(id+"F2.wireOp",EDGE,"E19.3.3")])]});
            var Q11;
            Q11=makeQuery(id+"F3.opExtrude","SWEPT_EDGE",EDGE,{"disambiguationData":[OSD([sQuery(id+"F2.wireOp",EDGE,"E19.3.2"),sQuery(id+"F2.wireOp",EDGE,"E19.3.3")])]});
            var Q12;
            Q12=makeQuery(id+"F3.opExtrude","SWEPT_EDGE",EDGE,{"disambiguationData":[OSD([sQuery(id+"F2.wireOp",EDGE,"E19.2.0"),sQuery(id+"F2.wireOp",EDGE,"E19.2.3")])]});
            var Q13;
            Q13=makeQuery(id+"F3.opExtrude","SWEPT_EDGE",EDGE,{"disambiguationData":[OSD([sQuery(id+"F2.wireOp",EDGE,"E19.2.2"),sQuery(id+"F2.wireOp",EDGE,"E19.2.3")])]});
            fillet(context, id + "F10", {"entities" : qUnion([Q0, Q1, Q2, Q3, Q4, Q5, Q6, Q7, Q8, Q9, Q10, Q11, Q12, Q13]), "radius" : 1 * mm, "tangentPropagation" : true, "allowEdgeOverflow" : false});
        }
    });
